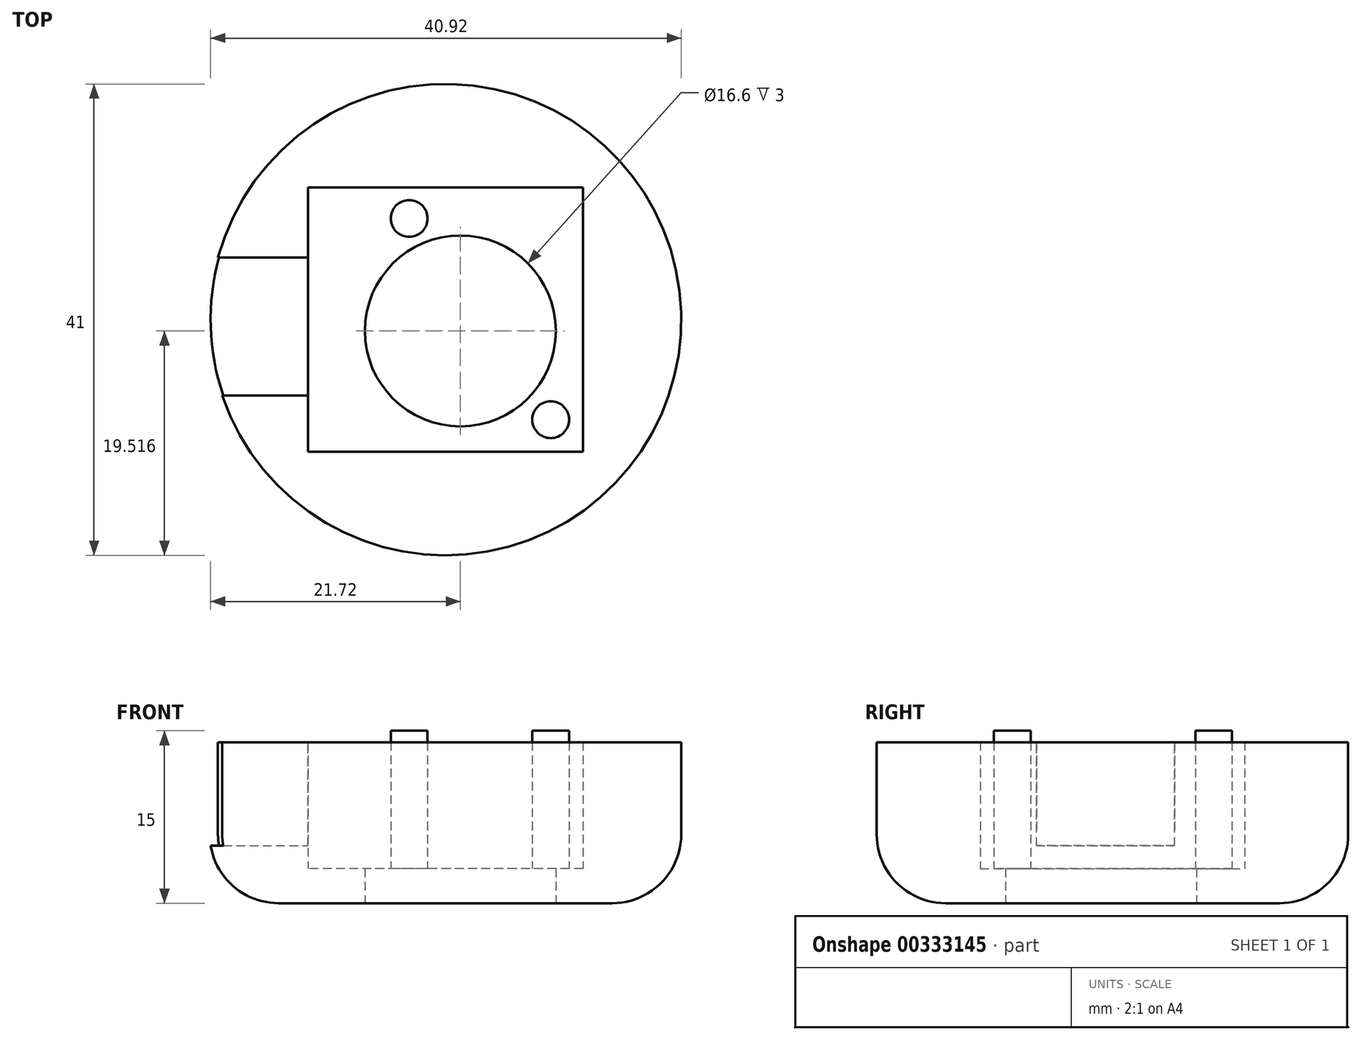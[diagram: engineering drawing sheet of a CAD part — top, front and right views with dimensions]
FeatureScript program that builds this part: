
annotation { "Feature Type Name" : "Feature", "Feature Type Description" : "" }
export const myFeature = defineFeature(function(context is Context, id is Id, definition is map)
    precondition{}
    {
        {
            var Q0;
            Q0=qCreatedBy(makeId("Top.planeOp"),FACE);
            var sketch = newSketch(context, id + "F0", { "sketchPlane" : qUnion([Q0])});
            skLineSegment(sketch, "E0.bottom", {"start": v(11.95, -11.5) * mm, "end": v(-11.95, -11.5) * mm});
            skLineSegment(sketch, "E0.top", {"start": v(11.95, 11.5) * mm, "end": v(-11.95, 11.5) * mm});
            skLineSegment(sketch, "E0.left", {"start": v(11.95, -11.5) * mm, "end": v(11.95, 11.5) * mm});
            skLineSegment(sketch, "E0.right", {"start": v(-11.95, -11.5) * mm, "end": v(-11.95, 11.5) * mm});
            skPoint(sketch, "E0.middle", {"position": v(0, 0) * mm});
            skCircle(sketch, "E1", {"center": v(0, 0) * mm, "radius": 20.5 * mm});
            skCircle(sketch, "E2", {"center": v(9.15, -8.7) * mm, "radius": 1.6 * mm});
            skCircle(sketch, "E3", {"center": v(-3.15, 8.8) * mm, "radius": 1.6 * mm});
            skCircle(sketch, "E4", {"center": v(-3.15, 8.8) * mm, "radius": 2.25 * mm});
            skCircle(sketch, "E5", {"center": v(9.15, -8.7) * mm, "radius": 2.25 * mm});
            skCircle(sketch, "E6", {"center": v(0, 0) * mm, "radius": 19 * mm});
            skSolve(sketch);
        }
        {
            var Q0;
            Q0=makeQuery(id+"F0.imprint","IMPRINT",FACE,{"disambiguationData":[TD([[makeQuery(id+"F0.imprint","IMPRINT",EDGE,{"derivedFrom":sQuery(id+"F0.wireOp",EDGE,"E0.bottom")}),-1.0]])]});
            var sketch = newSketch(context, id + "F1", { "sketchPlane" : qUnion([Q0])});
            skCircle(sketch, "E7", {"center": v(1.3, -0.98) * mm, "radius": 8.3 * mm});
            skSolve(sketch);
        }
        {
            var Q0;
            Q0=makeQuery(id+"F0.imprint","IMPRINT",FACE,{"disambiguationData":[TD([[makeQuery(id+"F0.imprint","IMPRINT",EDGE,{"derivedFrom":sQuery(id+"F0.wireOp",EDGE,"E1")}),1.0]])]});
            var Q1;
            Q1=makeQuery(id+"F0.imprint","IMPRINT",FACE,{"disambiguationData":[TD([[makeQuery(id+"F0.imprint","IMPRINT",EDGE,{"derivedFrom":sQuery(id+"F0.wireOp",EDGE,"E0.bottom")}),1.0]])]});
            extrude(context, id + "F2", {"entities" : qUnion([Q0, Q1]), "depth" : 14 * mm});
        }
        {
            var Q0;
            Q0=makeQuery(id+"F1.imprint","IMPRINT",FACE,{"disambiguationData":[TD([[makeQuery(id+"F1.imprint","IMPRINT",EDGE,{"derivedFrom":sQuery(id+"F1.wireOp",EDGE,"E7")}),-1.0]])]});
            var Q1;
            Q1=makeQuery(id+"F0.imprint","IMPRINT",FACE,{"disambiguationData":[TD([[makeQuery(id+"F0.imprint","IMPRINT",EDGE,{"derivedFrom":sQuery(id+"F0.wireOp",EDGE,"E3")}),-1.0]])]});
            var Q2;
            Q2=makeQuery(id+"F0.imprint","IMPRINT",FACE,{"disambiguationData":[TD([[makeQuery(id+"F0.imprint","IMPRINT",EDGE,{"derivedFrom":sQuery(id+"F0.wireOp",EDGE,"E3")}),1.0]])]});
            var Q3;
            Q3=makeQuery(id+"F0.imprint","IMPRINT",FACE,{"disambiguationData":[TD([[makeQuery(id+"F0.imprint","IMPRINT",EDGE,{"derivedFrom":sQuery(id+"F0.wireOp",EDGE,"E2")}),1.0]])]});
            var Q4;
            Q4=makeQuery(id+"F0.imprint","IMPRINT",FACE,{"disambiguationData":[TD([[makeQuery(id+"F0.imprint","IMPRINT",EDGE,{"derivedFrom":sQuery(id+"F0.wireOp",EDGE,"E2")}),-1.0]])]});
            extrude(context, id + "F3", {"entities" : qUnion([Q0, Q1, Q2, Q3, Q4]), "operationType" : NewBodyOperationType.ADD, "depth" : 3 * mm});
        }
        {
            var Q0;
            Q0=makeQuery(id+"F2.opExtrude","CAP_EDGE",EDGE,{"disambiguationData":[OSD([sQuery(id+"F0.wireOp",EDGE,"E1")])],"isStart":true});
            fillet(context, id + "F4", {"entities" : qUnion([Q0]), "radius" : 6 * mm, "tangentPropagation" : true, "allowEdgeOverflow" : false});
        }
        {
            var Q0;
            Q0=qCreatedBy(makeId("Right.planeOp"),FACE);
            var sketch = newSketch(context, id + "F5", { "sketchPlane" : qUnion([Q0])});
            skLineSegment(sketch, "E8.bottom", {"start": v(5.4, 8) * mm, "end": v(-6.6, 8) * mm});
            skLineSegment(sketch, "E8.top", {"start": v(5.4, 5) * mm, "end": v(-6.6, 5) * mm});
            skLineSegment(sketch, "E8.left", {"start": v(5.4, 8) * mm, "end": v(5.4, 5) * mm});
            skLineSegment(sketch, "E8.right", {"start": v(-6.6, 8) * mm, "end": v(-6.6, 5) * mm});
            skSolve(sketch);
        }
        {
            var Q0;
            Q0=makeQuery(id+"F0.imprint","IMPRINT",FACE,{"disambiguationData":[TD([[makeQuery(id+"F0.imprint","IMPRINT",EDGE,{"derivedFrom":sQuery(id+"F0.wireOp",EDGE,"E3")}),1.0]])]});
            var Q1;
            Q1=makeQuery(id+"F0.imprint","IMPRINT",FACE,{"disambiguationData":[TD([[makeQuery(id+"F0.imprint","IMPRINT",EDGE,{"derivedFrom":sQuery(id+"F0.wireOp",EDGE,"E2")}),1.0]])]});
            extrude(context, id + "F6", {"entities" : qUnion([Q0, Q1]), "operationType" : NewBodyOperationType.ADD, "depth" : 15 * mm});
        }
        {
            var Q0;
            Q0 = qSketchRegion(id + "F5", true);
            extrude(context, id + "F7", {"entities" : qUnion([Q0]), "operationType" : NewBodyOperationType.REMOVE, "oppositeDirection" : true, "depth" : 25 * mm});
        }
        {
            var Q0;
            Q0=makeQuery(id+"F7.boolean.opBoolean","COPY",FACE,{"derivedFrom":makeQuery(id+"F7.opExtrude","SWEPT_FACE",FACE,{"disambiguationData":[OSD([sQuery(id+"F5.wireOp",EDGE,"E8.bottom")])]})});
            extrude(context, id + "F8", {"entities" : qUnion([Q0]), "operationType" : NewBodyOperationType.REMOVE, "oppositeDirection" : true, "depth" : 25 * mm});
        }
    });
